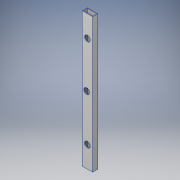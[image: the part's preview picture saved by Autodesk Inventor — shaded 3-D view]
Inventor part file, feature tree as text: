
AUTODESK INVENTOR PART (.ipt)
format: ipt  version: 2018 (Build 220112000, 112)  size: 128,000 bytes
history: native  units: in
note: dims shown in document units (in); Inventor stores cm internally (conversion verified against a paired STEP export)
features: extrude x3, sketch x3
ambient origin geometry x8: Origin, YZ Plane, XZ Plane, XY Plane, X Axis, Y Axis, Z Axis, Center Point
bodies: Solid1 (feature_tree)
feature tree (6):
  extrude  "Extrusion1"  Depth=1.0in
  extrude  "Extrusion2"  Depth=0.125in
  extrude  "Extrusion3"  Depth=0.125in
  sketch  "Sketch1"  dims[d0=2.0in d1=1.0in]
  sketch  "Sketch2"  dims[d2=0.125in d3=0.125in]
  sketch  "Sketch3"  dims[d4=0.125in d5=0.125in d6=26.0in d7=0.0in d9=1.0in d10=0.0in d11=0.125in d12=3.5in d13=3.5in d15=1.0in d16=0.0in d17=0.625in d18=0.625in]
